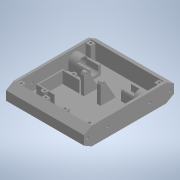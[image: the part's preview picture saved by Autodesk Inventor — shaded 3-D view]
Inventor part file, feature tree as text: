
AUTODESK INVENTOR PART (.ipt)
format: ipt  version: 2020 (Build 240168000, 168)  size: 475,648 bytes
history: native  units: in
note: dims shown in document units (in); Inventor stores cm internally (conversion verified against a paired STEP export)
features: extrude x14, sketch x14, projected_geometry x14, mirror x4, plane x1
ambient origin geometry x8: Origin, YZ Plane, XZ Plane, XY Plane, X Axis, Y Axis, Z Axis, Center Point
bodies: Solid1 (feature_tree)
feature tree (47):
  extrude  "Extrusion1"  Depth=5.9055in
  extrude  "Extrusion2"  TaperAngle=0.0deg  [1 undecoded]
  extrude  "Extrusion3"  Depth=1.063in
  extrude  "Extrusion4"  Depth=0.315in
  extrude  "Extrusion5"  TaperAngle=0.0deg  [1 undecoded]
  extrude  "Extrusion6"  Depth=0.5906in
  mirror  "Mirror1"
  extrude  "Extrusion7"  Depth=0.0787in
  mirror  "Mirror2"
  extrude  "Extrusion8"  Depth=0.6102in
  mirror  "Mirror3"
  plane  "Work Plane1"
  extrude  "Extrusion9"  Depth=0.7874in TaperAngle=0.0deg
  mirror  "Mirror4"
  extrude  "Extrusion10"  Depth=6.063in TaperAngle=0.0deg
  extrude  "Extrusion11"  Depth=0.1575in
  extrude  "Extrusion12"  TaperAngle=0.0deg  [1 undecoded]
  extrude  "Extrusion13"  Depth=0.2756in
  extrude  "Extrusion14"  Depth=0.4331in
  sketch  "Sketch1"  dims[d0=1.1811in d1=5.9055in]
  sketch  "Sketch2"  dims[d2=5.1181in d3=0.0in]
  projected_geometry  "Projected Loop1"
  sketch  "Sketch3"  dims[d4=0.1575in d5=1.063in]
  projected_geometry  "Projected Loop2"
  projected_geometry  "Projected Loop3"
  sketch  "Sketch4"  dims[d6=0.0in d8=0.315in]
  sketch  "Sketch5"  dims[d10=0.993in d11=0.0in]
  projected_geometry  "Projected Loop4"
  sketch  "Sketch6"  dims[d12=0.6496in d13=0.5906in]
  sketch  "Sketch7"  dims[d14=1.5748in d15=0.0787in]
  sketch  "Sketch9"  dims[d16=0.5512in d17=0.0in d18=0.6102in]
  sketch  "Sketch10"  dims[d19=0.4803in d20=0.7874in d21=0.0in]
  sketch  "Sketch12"  dims[d22=0.1654in d23=6.063in d24=0.0in]
  projected_geometry  "Projected Loop6"
  projected_geometry  "Projected Loop7"
  projected_geometry  "Projected Loop8"
  sketch  "Sketch13"  dims[d25=0.5114in d26=0.1575in]
  projected_geometry  "Projected Loop9"
  projected_geometry  "Projected Loop10"
  projected_geometry  "Projected Loop11"
  projected_geometry  "Projected Loop12"
  projected_geometry  "Projected Loop13"
  projected_geometry  "Projected Loop14"
  sketch  "Sketch14"  dims[d27=1.5748in d28=0.0in d29=0.0in]
  sketch  "Sketch15"  dims[d30=0.1575in d31=0.2756in]
  projected_geometry  "Projected Loop15"
  sketch  "Sketch16"  dims[d32=0.0in d33=0.4331in d34=0.122in d38=2.7559in d40=0.061in d41=0.0909in d42=0.2362in d43=0.0in d44=60.0deg d45=0.0787in d46=0.315in d48=0.993in d49=0.0in d51=0.1575in d52=0.1575in d53=0.2756in d54=0.0in d55=0.4724in d56=1.1614in d57=1.5748in d58=1.5945in d59=0.0787in d60=0.0787in d62=0.315in d63=0.7677in d64=0.0in d65=0.1575in d66=0.1575in d67=0.2756in d68=0.0in d69=0.8268in d70=0.2953in d71=0.0394in d72=0.0in]
note: 3 required parameter values undecoded (feature->parameter linkage not recoverable at this tier; creation-order binding heuristic only, values carry confidence <= 0.55)
